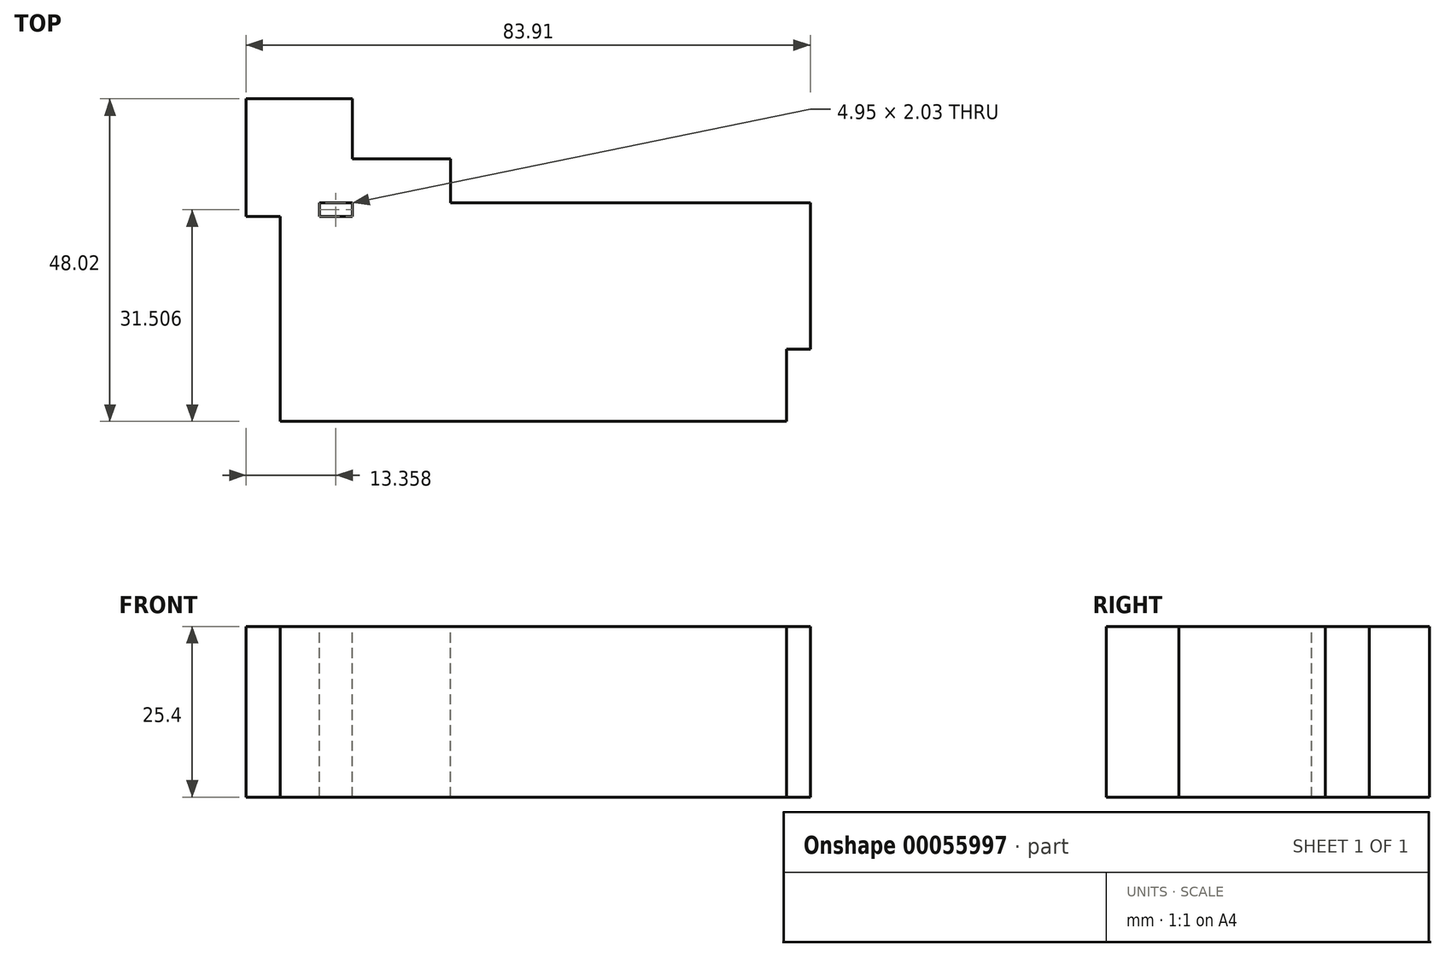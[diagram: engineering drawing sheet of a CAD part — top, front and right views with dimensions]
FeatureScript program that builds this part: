
annotation { "Feature Type Name" : "Feature", "Feature Type Description" : "" }
export const myFeature = defineFeature(function(context is Context, id is Id, definition is map)
    precondition{}
    {
        {
            var Q0;
            Q0=qCreatedBy(makeId("Top.planeOp"),FACE);
            var sketch = newSketch(context, id + "F0", { "sketchPlane" : qUnion([Q0])});
            skLineSegment(sketch, "E0.bottom", {"start": v(-49.63, 48.02) * mm, "end": v(-33.8, 48.02) * mm});
            skLineSegment(sketch, "E0.top", {"start": v(-49.63, 30.5) * mm, "end": v(-33.8, 30.5) * mm});
            skLineSegment(sketch, "E0.left", {"start": v(-49.63, 48.02) * mm, "end": v(-49.63, 30.5) * mm});
            skLineSegment(sketch, "E0.right", {"start": v(-33.8, 48.02) * mm, "end": v(-33.8, 30.5) * mm});
            skLineSegment(sketch, "E1.bottom", {"start": v(-38.75, 39.07) * mm, "end": v(-19.23, 39.07) * mm});
            skLineSegment(sketch, "E1.top", {"start": v(-38.75, 9.38) * mm, "end": v(-19.23, 9.38) * mm});
            skLineSegment(sketch, "E1.left", {"start": v(-38.75, 39.07) * mm, "end": v(-38.75, 9.38) * mm});
            skLineSegment(sketch, "E1.right", {"start": v(-19.23, 39.07) * mm, "end": v(-19.23, 9.38) * mm});
            skLineSegment(sketch, "E2.bottom", {"start": v(-44.56, 0) * mm, "end": v(30.75, 0) * mm});
            skLineSegment(sketch, "E2.top", {"start": v(-44.56, 32.52) * mm, "end": v(30.75, 32.52) * mm});
            skLineSegment(sketch, "E2.left", {"start": v(-44.56, 0) * mm, "end": v(-44.56, 32.52) * mm});
            skLineSegment(sketch, "E2.right", {"start": v(30.75, 0) * mm, "end": v(30.75, 32.52) * mm});
            skLineSegment(sketch, "E3.bottom", {"start": v(30.75, 32.52) * mm, "end": v(34.28, 32.52) * mm});
            skLineSegment(sketch, "E3.top", {"start": v(30.75, 10.74) * mm, "end": v(34.28, 10.74) * mm});
            skLineSegment(sketch, "E3.left", {"start": v(30.75, 32.52) * mm, "end": v(30.75, 10.74) * mm});
            skLineSegment(sketch, "E3.right", {"start": v(34.28, 32.52) * mm, "end": v(34.28, 10.74) * mm});
            skSolve(sketch);
        }
        {
            var Q0;
            Q0 = qSketchRegion(id + "F0", true);
            extrude(context, id + "F1", {"entities" : qUnion([Q0]), "oppositeDirection" : true, "depth" : 25.4 * mm});
        }
    });
